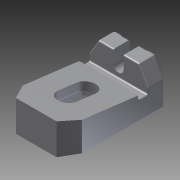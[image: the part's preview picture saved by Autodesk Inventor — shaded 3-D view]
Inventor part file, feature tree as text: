
AUTODESK INVENTOR PART (.ipt)
format: ipt  version: 2015 (Build 190159000, 159)  size: 483,840 bytes
history: native  units: mm (DEFAULTED — no unit token found)
features: sketch x11, extrude x10, fillet x2, plane x1
ambient origin geometry x8: Origin, YZ Plane, XZ Plane, XY Plane, X Axis, Y Axis, Z Axis, Center Point
bodies: Solid1 (feature_tree)
feature tree (24):
  extrude  "Extrusion1"  Depth=93.6625mm
  extrude  "Extrusion2"  TaperAngle=30.0deg  [1 undecoded]
  extrude  "Extrusion3"  Depth=250.825mm TaperAngle=0.0deg
  sketch  "Sketch4"  dims[d17=30.0deg d18=30.0deg]
  extrude  "Extrusion5"  TaperAngle=30.0deg  [1 undecoded]
  extrude  "Extrusion7"  Depth=250.825mm TaperAngle=0.0deg
  extrude  "Extrusion9"  Depth=136.525mm
  extrude  "Extrusion10"  Depth=69.85mm
  extrude  "Extrusion11"  Depth=44.45mm
  fillet  "Fillet1"  Radius=250.825mm
  extrude  "Extrusion12"  Depth=19.05mm
  plane  "Work Plane3"
  extrude  "Extrusion13"  Depth=38.1mm
  fillet  "Fillet3"  Radius=22.225mm
  sketch  "Sketch1"  dims[d0=139.7mm d1=93.6625mm]
  sketch  "Sketch2"  dims[d2=250.825mm d3=0.0mm d4=30.0deg]
  sketch  "Sketch3"  dims[d5=19.05mm d15=250.825mm d16=0.0mm]
  sketch  "Sketch5"  dims[d19=38.1mm d20=250.825mm d21=0.0mm]
  sketch  "Sketch7"  dims[d22=22.225mm d23=136.525mm]
  sketch  "Sketch8"  dims[d27=22.225mm d28=69.85mm]
  sketch  "Sketch9"  dims[d29=73.025mm d30=44.45mm d31=250.825mm d32=0.0mm]
  sketch  "Sketch10"  dims[d37=22.225mm d38=19.05mm]
  sketch  "Sketch11"  dims[d39=250.825mm d40=0.0mm d41=38.1mm d42=22.225mm]
  sketch  "Sketch12"  dims[d46=22.225mm d47=136.525mm d50=30.0deg d51=250.825mm d52=0.0mm d53=23.8125mm d54=69.85mm d55=63.5mm d56=250.825mm d57=0.0mm d58=19.05mm d59=19.05mm d60=250.825mm d61=0.0mm d62=3.175mm d64=41.275mm d66=304.8mm d67=38.1mm d68=73.025mm d69=25.4mm d70=0.0mm d71=-22.225mm d72=25.4mm d73=0.0mm d74=3.175mm]
note: 2 required parameter values undecoded (feature->parameter linkage not recoverable at this tier; creation-order binding heuristic only, values carry confidence <= 0.55)
